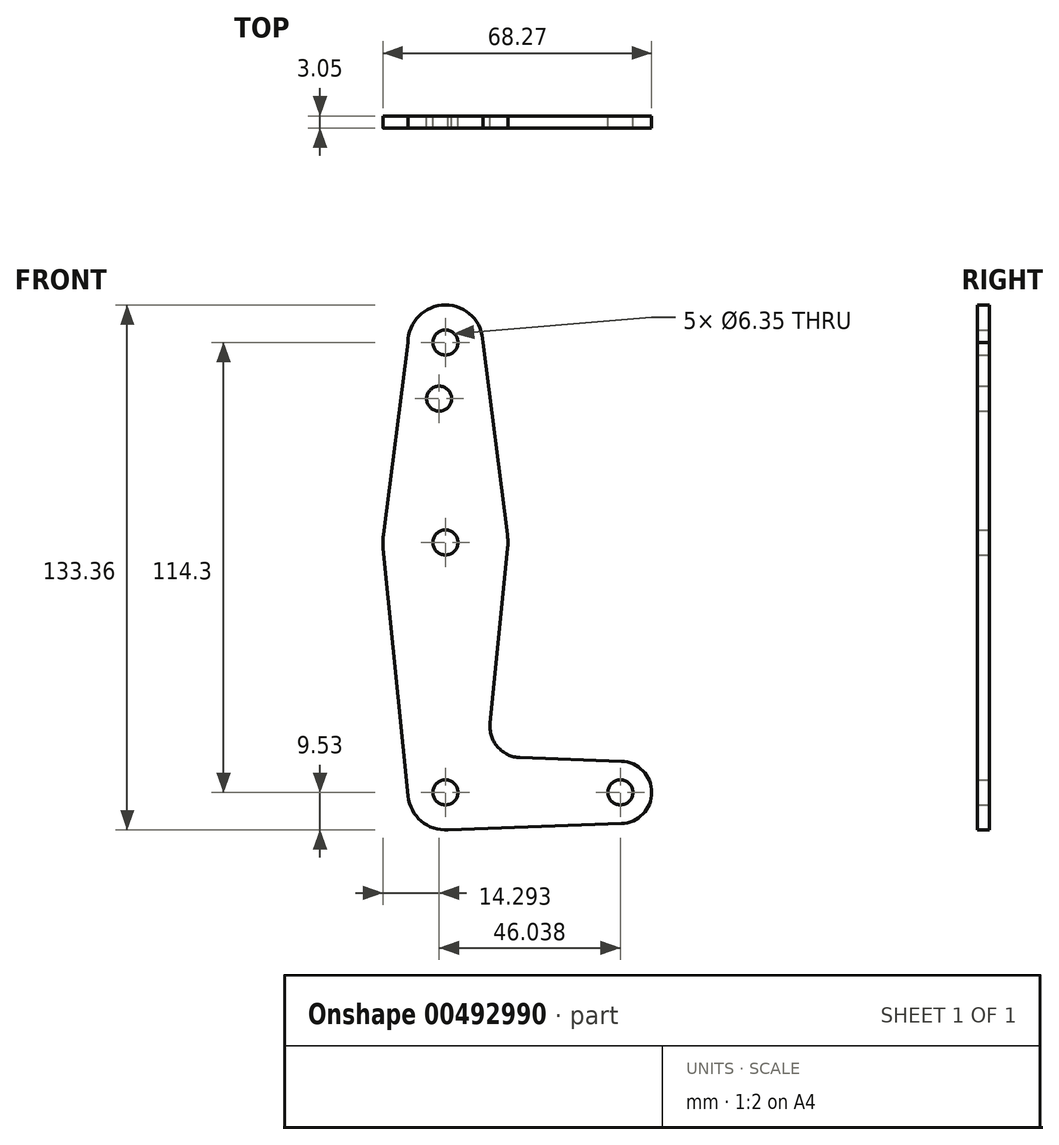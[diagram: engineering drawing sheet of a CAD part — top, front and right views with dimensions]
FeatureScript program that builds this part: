
annotation { "Feature Type Name" : "Feature", "Feature Type Description" : "" }
export const myFeature = defineFeature(function(context is Context, id is Id, definition is map)
    precondition{}
    {
        {
            var Q0;
            Q0=qCreatedBy(makeId("Front.planeOp"),FACE);
            var sketch = newSketch(context, id + "F0", { "sketchPlane" : qUnion([Q0])});
            skLineSegment(sketch, "E0", {"start": v(0, 0) * mm, "end": v(0, 114.3) * mm, "construction": true});
            skLineSegment(sketch, "E1", {"start": v(0, 0) * mm, "end": v(44.45, 0) * mm, "construction": true});
            skCircle(sketch, "E2", {"center": v(0, 114.3) * mm, "radius": 9.53 * mm});
            skCircle(sketch, "E3", {"center": v(0, 63.5) * mm, "radius": 15.88 * mm});
            skCircle(sketch, "E4", {"center": v(0, 0) * mm, "radius": 9.53 * mm});
            skCircle(sketch, "E5", {"center": v(44.45, 0) * mm, "radius": 7.94 * mm});
            skLineSegment(sketch, "E6", {"start": v(-9.52, 114.3) * mm, "end": v(-15.75, 65.5) * mm});
            skLineSegment(sketch, "E7", {"start": v(9.52, 114.3) * mm, "end": v(15.75, 65.5) * mm});
            skLineSegment(sketch, "E8", {"start": v(18.97, 8.85) * mm, "end": v(44.73, 7.93) * mm});
            skLineSegment(sketch, "E9", {"start": v(0, -9.53) * mm, "end": v(44.73, -7.93) * mm});
            skCircle(sketch, "E10", {"center": v(0, 114.3) * mm, "radius": 3.18 * mm});
            skCircle(sketch, "E11", {"center": v(-1.59, 100.03) * mm, "radius": 3.18 * mm});
            skCircle(sketch, "E12", {"center": v(0, 63.5) * mm, "radius": 3.18 * mm});
            skCircle(sketch, "E13", {"center": v(0, 0) * mm, "radius": 3.18 * mm});
            skCircle(sketch, "E14", {"center": v(44.45, 0) * mm, "radius": 3.18 * mm});
            skLineSegment(sketch, "E15", {"start": v(15.8, 61.91) * mm, "end": v(11.34, 17.59) * mm});
            skLineSegment(sketch, "E16", {"start": v(-15.8, 61.91) * mm, "end": v(-9.48, -0.95) * mm});
            skArc(sketch, "E17.filletArc", {"start": v(11.34, 17.59) * mm, "mid": v(13.26, 11.57) * mm, "end": v(18.97, 8.85) * mm});
            skSolve(sketch);
        }
        {
            var Q0;
            Q0 = qSketchRegion(id + "F0", true);
            var Q1;
            Q1 = qConstructionFilter(qBodyType(qCreatedBy(id + "F0" ,EDGE), BodyType.WIRE), ConstructionObject.NO);
            extrude(context, id + "F1", {"entities" : qUnion([Q0]), "surfaceEntities" : qUnion([Q1]), "depth" : 3.05 * mm});
        }
    });
